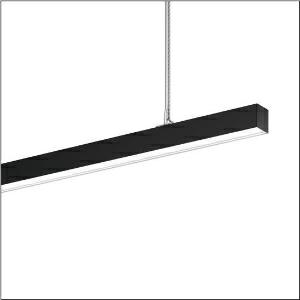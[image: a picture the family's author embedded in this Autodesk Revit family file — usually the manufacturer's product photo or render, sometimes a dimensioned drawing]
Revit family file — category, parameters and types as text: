
# Revit family: silica_r__21_51mx30db45bb_77a6
name_source: partatom
category: Lighting Fixtures
units: mm (PartAtom-declared; Revit-internal decimal feet)

## family parameters
Cut with Voids When Loaded = No
Host = Face
Light Source = No
Part Type = Normal
Room Calculation Point = No
Round Connector Dimension = Use Diameter
Shared = No

## types (1)
- --- (1 x LED, 5260 lm, 32 W, 4000K)
    Apparent Load = 32 VA
    CIE Flux Codes = 47 79 96 57 100
    Color Rendering = 80
    Color Temperature = 4000K
    Default Elevation = 1800 mm
    Description = Silica® 21, office luminaire, primary optical cover: cover, of PMMA, opal, light emission: direct/indirect distribution, primary light characteristic: symmetric, installation type: suspended mounting, LED, rated luminous flux: 5.260lm, luminous efficacy: 164lm/W, light colour: 840, colour temperature: 4000K, with terminal, 3+2-pole, max. 2.5mm², mains connection: 220..240V, AC, 50/60Hz, rated input power: 32W, luminaire housing, of aluminium, jet black (RAL 9005), length: 1.504mm, width: 53mm, height: 53mm, protection rating (complete): IP20, insulation class (complete): insulation class I (protective earthing), certification: CE, permissible operating ambient temperature: 0..+35°C, standard: EN 50419, packaging unit: 1 piece
    Height = 53 mm
    Lamp = 1 x LED
    Lamp Light Flux = 5260 lm
    Lamp Power = 32 W
    Lamp count = 1
    Length = 1504 mm
    Luminous efficacy = 164 lm/W
    Manufacturer = Siteco
    ModVariant = No
    Model = 51MX30DB45BB
    Mounting Place = Ceiling
    Mounting Type = Pendant
    Number of Poles = 1
    OnlyDefault = Yes
    Power Factor = 1
    Product Name = Silica® 21
    Product group = office luminaire | ceiling pendant
    ProductGroupID = 902
    Protection Class = Protection class I
    Protection Degree = IP 20
    RLX_Detail_Level = 1
    RLX_Emergency_Light_Flux = 0 lm
    RLX_Emergency_Type = 0
    RLX_Emergency_Type_DB = No
    RlxData = <blob elided: 26041 chars, md5=15772a9b>
    Socket = socket
    Standby Power = 0 W
    System Light Flux = 5260 lm
    System Power = 32 W
    Type Comments = factory setting: luminous flux: 100 % | dim-lin: 254 | 218 mA
    Type Image = l_1335856.jpg
    URL = http://relux.com
    VarID = @adj_085867
    Voltage = 0 V
    Weight = 0.00 kg
    Width = 53 mm

## geometry (parser evidence)
native form markers: Blend x4, Sweep x13
no freeform markers — native parametric forms only
